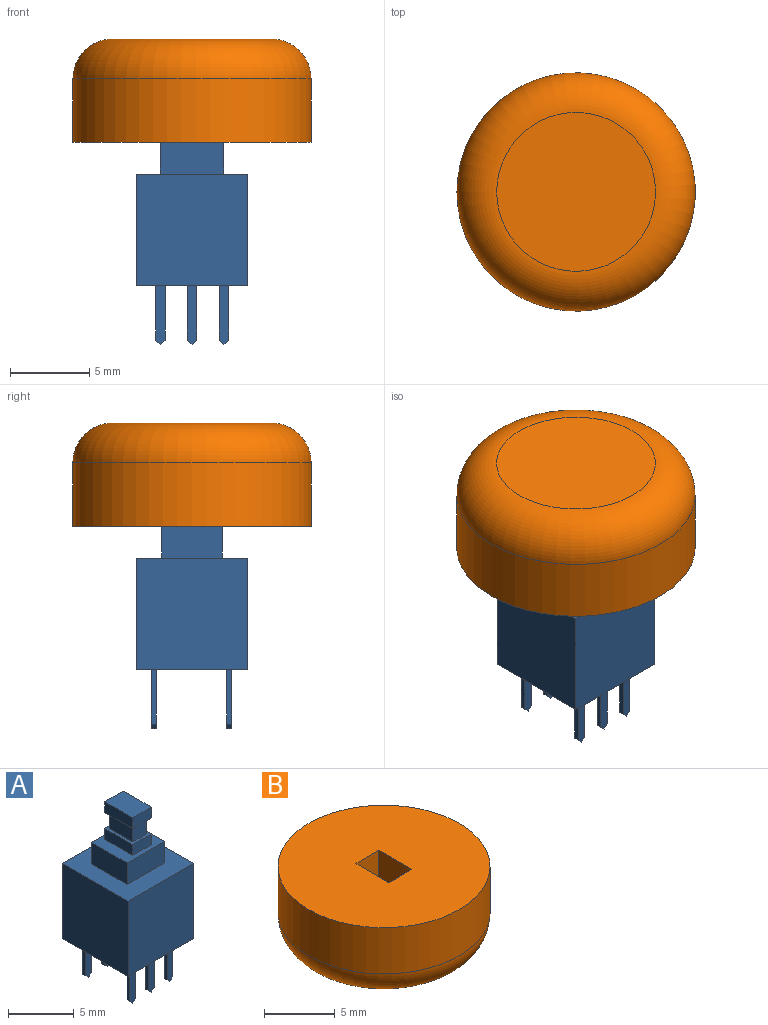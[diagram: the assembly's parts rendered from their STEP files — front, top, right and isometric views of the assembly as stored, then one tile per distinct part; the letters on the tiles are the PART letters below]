
ASSEMBLY  parts=2 mates=1
PART A: 62 faces, bbox 7x7x16.3 mm
  f0: plane 7x7mm, normal (0,0,1), area 33.8mm2, adj f1,f2,f3,f4,f7,f8,f9,f10
  f1: plane 7x7mm, normal (0,-1,0), area 49mm2, adj f0,f2,f4,f5
  f2: plane 7x7mm, normal (1,0,0), area 49mm2, adj f0,f1,f3,f5
  f3: plane 7x7mm, normal (0,1,0), area 49mm2, adj f0,f2,f4,f5
  f4: plane 7x7mm, normal (-1,0,0), area 49mm2, adj f0,f1,f3,f5
  f5: plane 7x7mm, normal (0,0,-1), area 47.9mm2, adj f1,f2,f3,f4,f26,f27,f28,f29
  f6: plane 4x3.8mm, normal (0,0,1), area 9.2mm2, adj f7,f8,f9,f10,f12,f13,f14,f15
  f7: plane 4x2mm, normal (0,-1,0), area 8mm2, adj f0,f6,f8,f10
  f8: plane 3.8x2mm, normal (1,0,0), area 7.6mm2, adj f0,f6,f7,f9
  f9: plane 4x2mm, normal (0,1,0), area 8mm2, adj f0,f6,f8,f10
  f10: plane 3.8x2mm, normal (-1,0,0), area 7.6mm2, adj f0,f6,f7,f9
  f11: plane 3x2mm, normal (0,0,1), area 2.2mm2, adj f12,f13,f14,f15,f16,f17,f18,f19
  f12: plane 2x1mm, normal (0,-1,0), area 2mm2, adj f6,f11,f13,f15
  f13: plane 3x1mm, normal (1,0,0), area 3mm2, adj f6,f11,f12,f14
  f14: plane 2x1mm, normal (0,1,0), area 2mm2, adj f6,f11,f13,f15
  f15: plane 3x1mm, normal (-1,0,0), area 3mm2, adj f6,f11,f12,f14
  f16: plane 1.5x1.5mm, normal (0,-1,0), area 2.2mm2, adj f11,f17,f19,f25
  f17: plane 2.5x1.5mm, normal (1,0,0), area 3.7mm2, adj f11,f16,f18,f25
  f18: plane 1.5x1.5mm, normal (0,1,0), area 2.2mm2, adj f11,f17,f19,f25
  f19: plane 2.5x1.5mm, normal (-1,0,0), area 3.7mm2, adj f11,f16,f18,f25
  f20: plane 2x1mm, normal (0,-1,0), area 2mm2, adj f21,f23,f24,f25
  f21: plane 3x1mm, normal (1,0,0), area 3mm2, adj f20,f22,f24,f25
  f22: plane 2x1mm, normal (0,1,0), area 2mm2, adj f21,f23,f24,f25
  f23: plane 3x1mm, normal (-1,0,0), area 3mm2, adj f20,f22,f24,f25
  f24: plane 3x2mm, normal (0,0,1), area 6mm2, adj f20,f21,f22,f23
  f25: plane 3x2mm, normal (0,0,-1), area 2.2mm2, adj f16,f17,f18,f19,f20,f21,f22,f23
  f26: plane 3.75x0.6mm, normal (0,1,0), area 2.2mm2, adj f5,f27,f29,f30,f31
  f27: plane 3.45x0.3mm, normal (1,0,0), area 1mm2, adj f5,f26,f28,f31
  f28: plane 3.75x0.6mm, normal (0,-1,0), area 2.2mm2, adj f5,f27,f29,f30,f31
  f29: plane 3.45x0.3mm, normal (-1,0,0), area 1mm2, adj f5,f26,f28,f30
  f30: plane 0.3x0.3mm, normal (-0.71,0,-0.71), area 0.1mm2, adj f26,f28,f29,f31
  f31: plane 0.3x0.3mm, normal (0.71,0,-0.71), area 0.1mm2, adj f26,f27,f28,f30
  f32: plane 3.75x0.6mm, normal (0,1,0), area 2.2mm2, adj f5,f33,f35,f36,f37
  f33: plane 3.45x0.3mm, normal (1,0,0), area 1mm2, adj f5,f32,f34,f37
  f34: plane 3.75x0.6mm, normal (0,-1,0), area 2.2mm2, adj f5,f33,f35,f36,f37
  f35: plane 3.45x0.3mm, normal (-1,0,0), area 1mm2, adj f5,f32,f34,f36
  f36: plane 0.3x0.3mm, normal (-0.71,0,-0.71), area 0.1mm2, adj f32,f34,f35,f37
  f37: plane 0.3x0.3mm, normal (0.71,0,-0.71), area 0.1mm2, adj f32,f33,f34,f36
  f38: plane 3.75x0.6mm, normal (0,1,0), area 2.2mm2, adj f5,f39,f41,f42,f43
  f39: plane 3.45x0.3mm, normal (1,0,0), area 1mm2, adj f5,f38,f40,f43
  f40: plane 3.75x0.6mm, normal (0,-1,0), area 2.2mm2, adj f5,f39,f41,f42,f43
  f41: plane 3.45x0.3mm, normal (-1,0,0), area 1mm2, adj f5,f38,f40,f42
  f42: plane 0.3x0.3mm, normal (-0.71,0,-0.71), area 0.1mm2, adj f38,f40,f41,f43
  f43: plane 0.3x0.3mm, normal (0.71,0,-0.71), area 0.1mm2, adj f38,f39,f40,f42
  f44: plane 3.75x0.6mm, normal (0,1,0), area 2.2mm2, adj f5,f45,f47,f48,f49
  f45: plane 3.45x0.3mm, normal (1,0,0), area 1mm2, adj f5,f44,f46,f49
  f46: plane 3.75x0.6mm, normal (0,-1,0), area 2.2mm2, adj f5,f45,f47,f48,f49
  f47: plane 3.45x0.3mm, normal (-1,0,0), area 1mm2, adj f5,f44,f46,f48
  f48: plane 0.3x0.3mm, normal (-0.71,0,-0.71), area 0.1mm2, adj f44,f46,f47,f49
  f49: plane 0.3x0.3mm, normal (0.71,0,-0.71), area 0.1mm2, adj f44,f45,f46,f48
  f50: plane 3.75x0.6mm, normal (0,1,0), area 2.2mm2, adj f5,f51,f53,f54,f55
  f51: plane 3.45x0.3mm, normal (1,0,0), area 1mm2, adj f5,f50,f52,f55
  f52: plane 3.75x0.6mm, normal (0,-1,0), area 2.2mm2, adj f5,f51,f53,f54,f55
  f53: plane 3.45x0.3mm, normal (-1,0,0), area 1mm2, adj f5,f50,f52,f54
  f54: plane 0.3x0.3mm, normal (-0.71,0,-0.71), area 0.1mm2, adj f50,f52,f53,f55
  f55: plane 0.3x0.3mm, normal (0.71,0,-0.71), area 0.1mm2, adj f50,f51,f52,f54
  f56: plane 3.75x0.6mm, normal (0,1,0), area 2.2mm2, adj f5,f57,f59,f60,f61
  f57: plane 3.45x0.3mm, normal (1,0,0), area 1mm2, adj f5,f56,f58,f61
  f58: plane 3.75x0.6mm, normal (0,-1,0), area 2.2mm2, adj f5,f57,f59,f60,f61
  f59: plane 3.45x0.3mm, normal (-1,0,0), area 1mm2, adj f5,f56,f58,f60
  f60: plane 0.3x0.3mm, normal (-0.71,0,-0.71), area 0.1mm2, adj f56,f58,f59,f61
  f61: plane 0.3x0.3mm, normal (0.71,0,-0.71), area 0.1mm2, adj f56,f57,f58,f60
PART B: 9 faces, bbox 16.2x16.2x6.5 mm
  f0: plane 3.5x2.3mm, normal (0,1,0), area 8.1mm2, adj f1,f3,f5,f6
  f1: plane 3.5x3.3mm, normal (-1,0,0), area 11.6mm2, adj f0,f2,f5,f6
  f2: plane 3.5x2.3mm, normal (0,-1,0), area 8.1mm2, adj f1,f3,f5,f6
  f3: plane 3.5x3.3mm, normal (1,0,0), area 11.6mm2, adj f0,f2,f5,f6
  f4: cylinder r=7.5mm len=15mm, axis (0,0,-1), area 188.5mm2, adj f5,f8
  f5: plane 15x15mm, normal (0,0,1), area 169.1mm2, adj f0,f1,f2,f3,f4
  f6: plane 3.3x2.3mm, normal (0,0,1), area 7.6mm2, adj f0,f1,f2,f3
  f7: plane 10x10mm, normal (0,0,-1), area 78.5mm2, adj f8
  f8: torus R=5mm, axis (0,0,-1), area 162.6mm2, adj f4,f7
PLACE A t=(0,0,4)mm
PLACE B rot(axis=(1,0,0),180deg) t=(0,0,0)mm
MATE fastened A.f24 <-> B.f4  axis (0,0,1) through (0,0,16.5)mm
